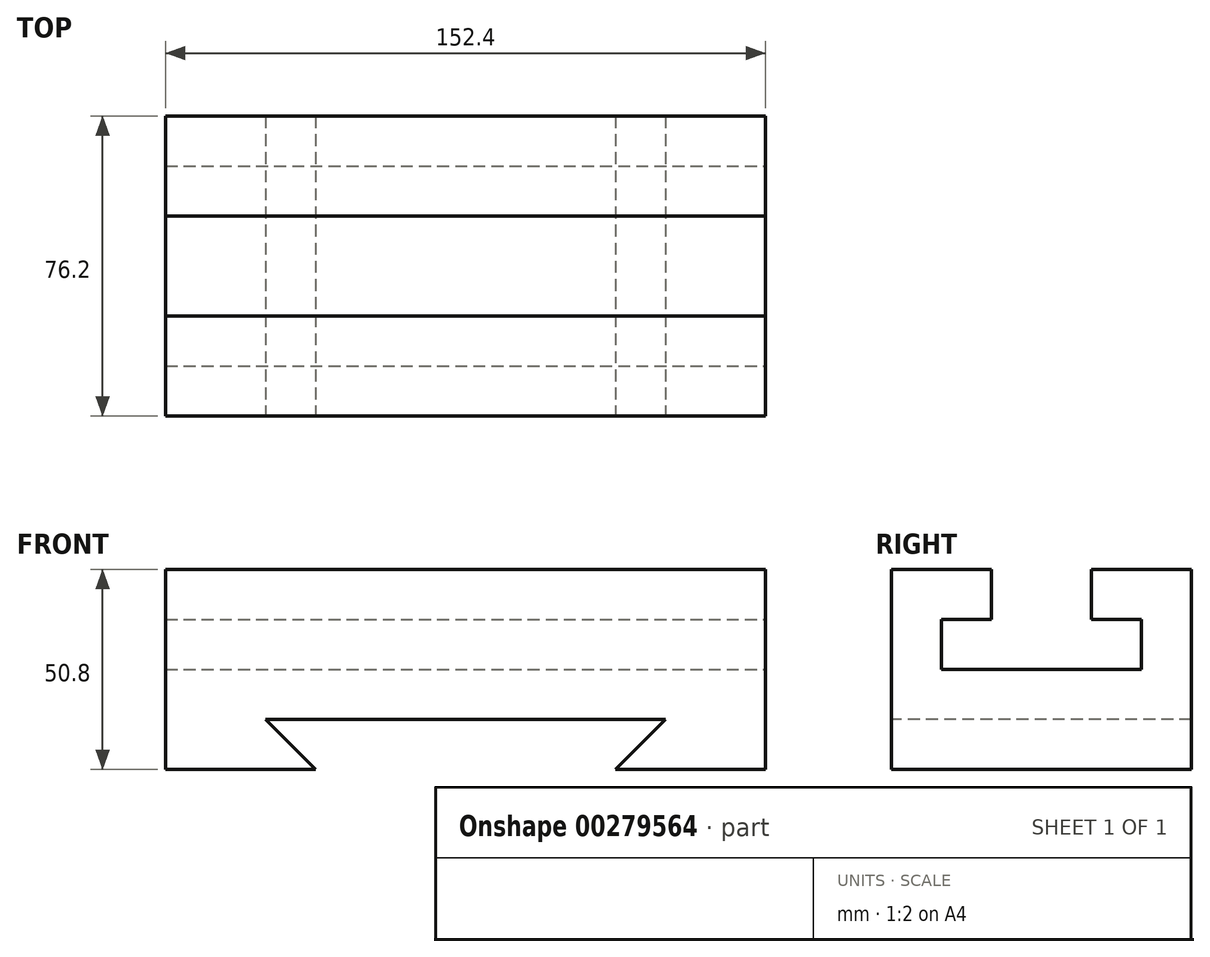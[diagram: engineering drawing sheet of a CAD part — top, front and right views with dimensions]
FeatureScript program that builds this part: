
annotation { "Feature Type Name" : "Feature", "Feature Type Description" : "" }
export const myFeature = defineFeature(function(context is Context, id is Id, definition is map)
    precondition{}
    {
        {
            var Q0;
            Q0=qCreatedBy(makeId("Front.planeOp"),FACE);
            var sketch = newSketch(context, id + "F0", { "sketchPlane" : qUnion([Q0])});
            skLineSegment(sketch, "E0.bottom", {"start": v(-76.2, 25.4) * mm, "end": v(76.2, 25.4) * mm});
            skLineSegment(sketch, "E0.top", {"start": v(-76.2, -25.4) * mm, "end": v(76.2, -25.4) * mm});
            skLineSegment(sketch, "E0.left", {"start": v(-76.2, 25.4) * mm, "end": v(-76.2, -25.4) * mm});
            skLineSegment(sketch, "E0.right", {"start": v(76.2, 25.4) * mm, "end": v(76.2, -25.4) * mm});
            skPoint(sketch, "E0.middle", {"position": v(0, 0) * mm});
            skSolve(sketch);
        }
        {
            var Q0;
            Q0=makeQuery(id+"F0.imprint","IMPRINT",FACE,{"disambiguationData":[TD([[makeQuery(id+"F0.imprint","IMPRINT",EDGE,{"derivedFrom":sQuery(id+"F0.wireOp",EDGE,"E0.bottom")}),-1.0]])]});
            extrude(context, id + "F1", {"entities" : qUnion([Q0]), "depth" : 38.1 * mm});
        }
        {
            var Q0;
            Q0=makeQuery(id+"F1.opExtrude","CAP_FACE",FACE,{"disambiguationData":[OSD([sQuery(id+"F0.wireOp",EDGE,"E0.bottom"),sQuery(id+"F0.wireOp",EDGE,"E0.top"),sQuery(id+"F0.wireOp",EDGE,"E0.left"),sQuery(id+"F0.wireOp",EDGE,"E0.right")])],"isStart":true});
            extrude(context, id + "F2", {"entities" : qUnion([Q0]), "operationType" : NewBodyOperationType.ADD, "depth" : 38.1 * mm});
        }
        {
            var Q0;
            Q0=makeQuery(id+"F1.opExtrude","CAP_FACE",FACE,{"disambiguationData":[OSD([sQuery(id+"F0.wireOp",EDGE,"E0.bottom"),sQuery(id+"F0.wireOp",EDGE,"E0.top"),sQuery(id+"F0.wireOp",EDGE,"E0.left"),sQuery(id+"F0.wireOp",EDGE,"E0.right")])],"isStart":false});
            var sketch = newSketch(context, id + "F3", { "sketchPlane" : qUnion([Q0])});
            skLineSegment(sketch, "E1", {"start": v(-50.8, -12.7) * mm, "end": v(-38.1, -25.4) * mm});
            skLineSegment(sketch, "E2", {"start": v(50.8, -12.7) * mm, "end": v(38.1, -25.4) * mm});
            skLineSegment(sketch, "E3", {"start": v(50.8, -12.7) * mm, "end": v(-50.8, -12.7) * mm});
            skSolve(sketch);
        }
        {
            var Q0;
            {var subQ0=sQuery(id+"F3.wireOp",EDGE,"E1");Q0=makeQuery(id+"F3.imprint","IMPRINT",FACE,{"disambiguationData":[TD([[makeQuery(id+"F3.imprint","IMPRINT",EDGE,{"derivedFrom":subQ0}),1.0]])]});}
            extrude(context, id + "F4", {"entities" : qUnion([Q0]), "operationType" : NewBodyOperationType.REMOVE, "oppositeDirection" : true, "depth" : 76.2 * mm});
        }
        {
            var Q0;
            {var subQ0=sQuery(id+"F0.wireOp",EDGE,"E0.right");Q0=makeQuery(id+"F2.boolean.opBoolean","MERGE",FACE,{"derivedFrom":[makeQuery(id+"F1.opExtrude","SWEPT_FACE",FACE,{"disambiguationData":[OSD([subQ0])]}),makeQuery(id+"F2.opExtrude","SWEPT_FACE",FACE,{"disambiguationData":[OSD([subQ0])]})]});}
            var sketch = newSketch(context, id + "F5", { "sketchPlane" : qUnion([Q0])});
            skLineSegment(sketch, "E4", {"start": v(-38.1, -25.4) * mm, "end": v(-38.1, 12.7) * mm});
            skLineSegment(sketch, "E5", {"start": v(38.1, -25.4) * mm, "end": v(38.1, 12.7) * mm});
            skLineSegment(sketch, "E6", {"start": v(-38.1, 12.7) * mm, "end": v(-38.1, 0) * mm});
            skLineSegment(sketch, "E7", {"start": v(38.1, 12.7) * mm, "end": v(38.1, 0) * mm});
            skLineSegment(sketch, "E8", {"start": v(38.1, 25.4) * mm, "end": v(12.7, 25.4) * mm});
            skLineSegment(sketch, "E9", {"start": v(-38.1, 25.4) * mm, "end": v(-12.7, 25.4) * mm});
            skLineSegment(sketch, "E10", {"start": v(-12.7, 25.4) * mm, "end": v(-12.7, 12.7) * mm});
            skLineSegment(sketch, "E11", {"start": v(12.7, 25.4) * mm, "end": v(12.7, 12.7) * mm});
            skLineSegment(sketch, "E12", {"start": v(12.7, 12.7) * mm, "end": v(25.4, 12.7) * mm});
            skLineSegment(sketch, "E13", {"start": v(-12.7, 12.7) * mm, "end": v(-25.4, 12.7) * mm});
            skLineSegment(sketch, "E14", {"start": v(-25.4, 12.7) * mm, "end": v(-25.4, 0) * mm});
            skLineSegment(sketch, "E15", {"start": v(25.4, 12.7) * mm, "end": v(25.4, 0) * mm});
            skLineSegment(sketch, "E16", {"start": v(-25.4, 0) * mm, "end": v(25.4, 0) * mm});
            skSolve(sketch);
        }
        {
            var Q0;
            {var subQ1=sQuery(id+"F5.wireOp",EDGE,"E10");Q0=makeQuery(id+"F5.imprint","IMPRINT",FACE,{"disambiguationData":[TD([[makeQuery(id+"F5.imprint","IMPRINT",EDGE,{"derivedFrom":subQ1}),1.0]])]});}
            extrude(context, id + "F6", {"entities" : qUnion([Q0]), "operationType" : NewBodyOperationType.REMOVE, "oppositeDirection" : true, "depth" : 152.4 * mm});
        }
    });
